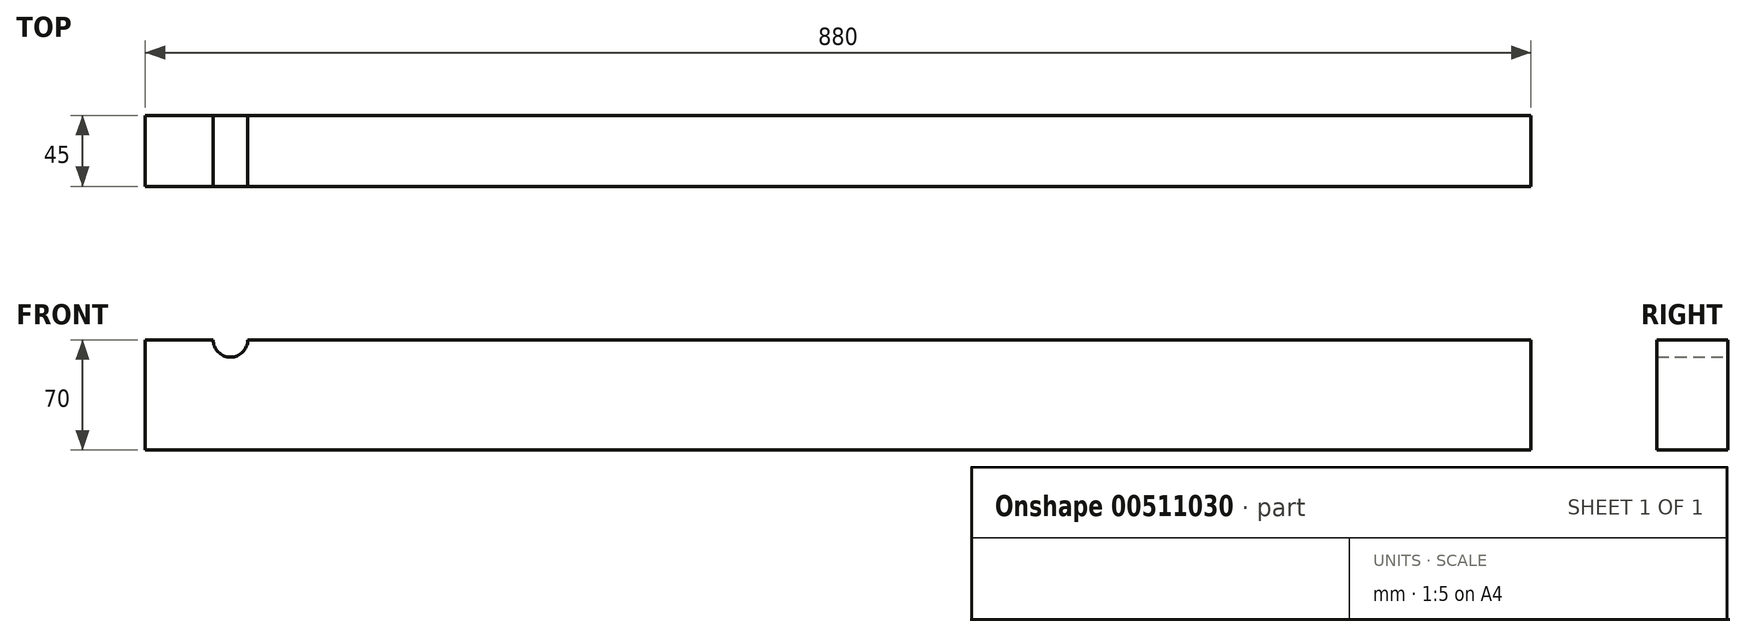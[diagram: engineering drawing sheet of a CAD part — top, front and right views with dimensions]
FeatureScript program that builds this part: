
annotation { "Feature Type Name" : "Feature", "Feature Type Description" : "" }
export const myFeature = defineFeature(function(context is Context, id is Id, definition is map)
    precondition{}
    {
        {
            var Q0;
            Q0=qCreatedBy(makeId("Front.planeOp"),FACE);
            var sketch = newSketch(context, id + "F0", { "sketchPlane" : qUnion([Q0])});
            skLineSegment(sketch, "E0.bottom", {"start": v(0, 0) * mm, "end": v(-815, 0) * mm});
            skLineSegment(sketch, "E0.top", {"start": v(0, -70) * mm, "end": v(-880, -70) * mm});
            skLineSegment(sketch, "E0.left", {"start": v(0, 0) * mm, "end": v(0, -70) * mm});
            skLineSegment(sketch, "E0.right", {"start": v(-880, 0) * mm, "end": v(-880, -70) * mm});
            skArc(sketch, "E1", {"start": v(-837, 0) * mm, "mid": v(-826, -11) * mm, "end": v(-815, 0) * mm});
            skLineSegment(sketch, "E2.trimOffspring", {"start": v(-837, 0) * mm, "end": v(-880, 0) * mm});
            skSolve(sketch);
        }
        {
            var Q0;
            Q0=qSketchRegion(id+"F0",true);
            extrude(context, id + "F1", {"entities" : qUnion([Q0]), "depth" : 45 * mm});
        }
    });
